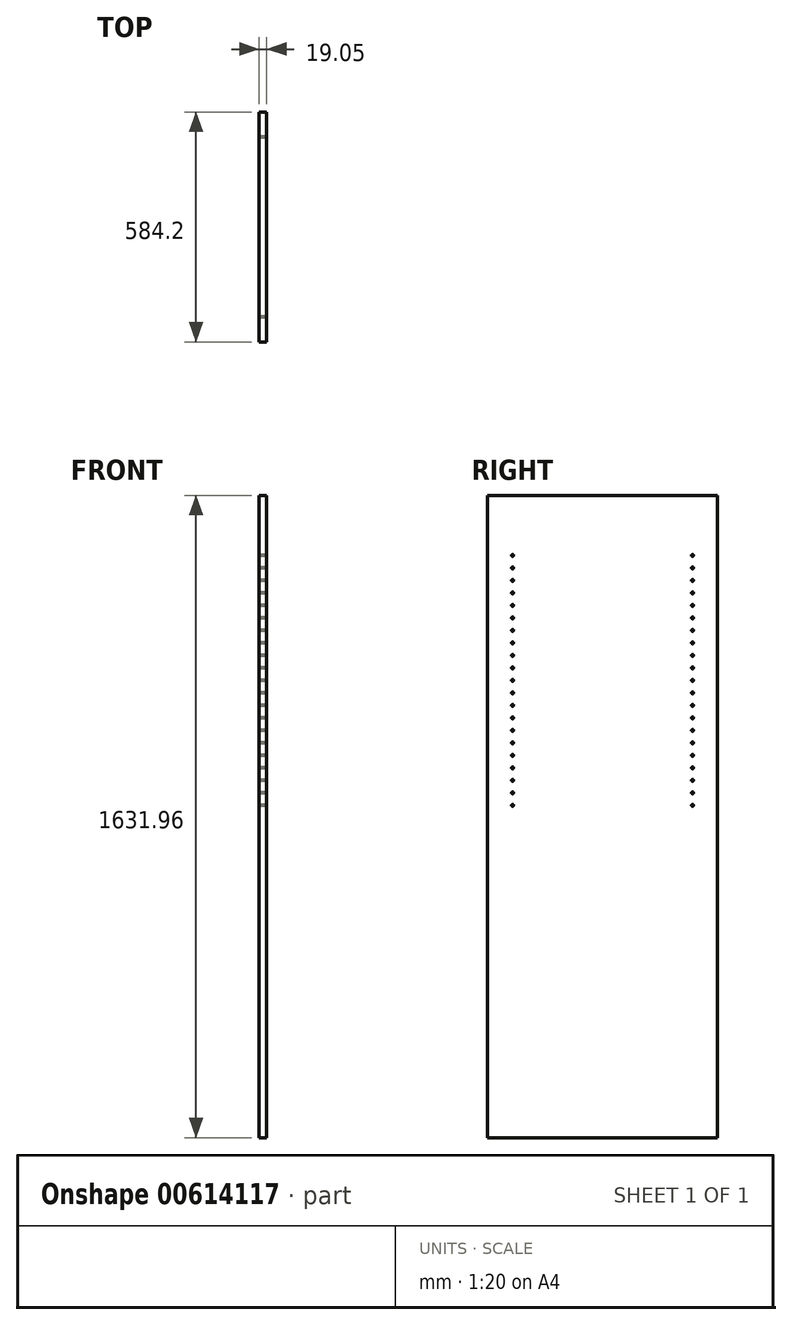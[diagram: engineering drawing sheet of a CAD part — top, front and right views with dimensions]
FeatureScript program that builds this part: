
annotation { "Feature Type Name" : "Feature", "Feature Type Description" : "" }
export const myFeature = defineFeature(function(context is Context, id is Id, definition is map)
    precondition{}
    {
        {
            var Q0;
            Q0=qCreatedBy(makeId("Right.planeOp"),FACE);
            var sketch = newSketch(context, id + "F0", { "sketchPlane" : qUnion([Q0])});
            skLineSegment(sketch, "E0.bottom", {"start": v(292.1, 815.98) * mm, "end": v(-292.1, 815.98) * mm});
            skLineSegment(sketch, "E0.top", {"start": v(292.1, -815.98) * mm, "end": v(-292.1, -815.98) * mm});
            skLineSegment(sketch, "E0.left", {"start": v(292.1, 815.98) * mm, "end": v(292.1, -815.98) * mm});
            skLineSegment(sketch, "E0.right", {"start": v(-292.1, 815.98) * mm, "end": v(-292.1, -815.98) * mm});
            skPoint(sketch, "E0.middle", {"position": v(0, 0) * mm});
            skSolve(sketch);
        }
        {
            var Q0;
            Q0=makeQuery(id+"F0.imprint","IMPRINT",FACE,{"disambiguationData":[TD([[makeQuery(id+"F0.imprint","IMPRINT",EDGE,{"derivedFrom":sQuery(id+"F0.wireOp",EDGE,"E0.bottom")}),1.0]])]});
            extrude(context, id + "F1", {"entities" : qUnion([Q0]), "depth" : 19.05 * mm, "offsetDistance" : 25.4 * mm});
        }
        {
            var Q0;
            Q0=makeQuery(id+"F1.opExtrude","CAP_FACE",FACE,{"disambiguationData":[OSD([sQuery(id+"F0.wireOp",EDGE,"E0.bottom"),sQuery(id+"F0.wireOp",EDGE,"E0.top"),sQuery(id+"F0.wireOp",EDGE,"E0.left"),sQuery(id+"F0.wireOp",EDGE,"E0.right")])],"isStart":false});
            var sketch = newSketch(context, id + "F2", { "sketchPlane" : qUnion([Q0])});
            skLineSegment(sketch, "E1", {"start": v(0, -815.98) * mm, "end": v(0, -53.97) * mm});
            skPoint(sketch, "E1.endSnap0", {"position": v(0, -815.98) * mm});
            skLineSegment(sketch, "E2", {"start": v(0, -53.97) * mm, "end": v(-292.1, -53.97) * mm});
            skLineSegment(sketch, "E3", {"start": v(0, 815.98) * mm, "end": v(0, 631.83) * mm});
            skPoint(sketch, "E3.endSnap0", {"position": v(0, 815.98) * mm});
            skLineSegment(sketch, "E4.bottom", {"start": v(228.6, 600.08) * mm, "end": v(-228.6, 600.08) * mm});
            skLineSegment(sketch, "E4.top", {"start": v(228.6, 663.58) * mm, "end": v(-228.6, 663.58) * mm});
            skLineSegment(sketch, "E4.left", {"start": v(228.6, 600.08) * mm, "end": v(228.6, 663.58) * mm});
            skLineSegment(sketch, "E4.right", {"start": v(-228.6, 600.08) * mm, "end": v(-228.6, 663.58) * mm});
            skPoint(sketch, "E4.middle", {"position": v(0, 631.83) * mm});
            skLineSegment(sketch, "E5", {"start": v(0, 600.08) * mm, "end": v(0, 536.58) * mm});
            skLineSegment(sketch, "E6.bottom", {"start": v(228.6, 568.33) * mm, "end": v(-228.6, 568.33) * mm});
            skLineSegment(sketch, "E6.top", {"start": v(228.6, 504.83) * mm, "end": v(-228.6, 504.83) * mm});
            skLineSegment(sketch, "E6.left", {"start": v(228.6, 568.33) * mm, "end": v(228.6, 504.83) * mm});
            skLineSegment(sketch, "E6.right", {"start": v(-228.6, 568.33) * mm, "end": v(-228.6, 504.83) * mm});
            skPoint(sketch, "E6.middle", {"position": v(0, 536.58) * mm});
            skLineSegment(sketch, "E7", {"start": v(0, 504.83) * mm, "end": v(0, 441.33) * mm});
            skLineSegment(sketch, "E8.bottom", {"start": v(228.6, 409.58) * mm, "end": v(-228.6, 409.58) * mm});
            skLineSegment(sketch, "E8.top", {"start": v(228.6, 473.08) * mm, "end": v(-228.6, 473.08) * mm});
            skLineSegment(sketch, "E8.left", {"start": v(228.6, 409.58) * mm, "end": v(228.6, 473.08) * mm});
            skLineSegment(sketch, "E8.right", {"start": v(-228.6, 409.58) * mm, "end": v(-228.6, 473.08) * mm});
            skPoint(sketch, "E8.middle", {"position": v(0, 441.33) * mm});
            skLineSegment(sketch, "E9", {"start": v(0, 409.58) * mm, "end": v(0, 346.08) * mm});
            skLineSegment(sketch, "E10.bottom", {"start": v(228.6, 377.83) * mm, "end": v(-228.6, 377.83) * mm});
            skLineSegment(sketch, "E10.top", {"start": v(228.6, 314.33) * mm, "end": v(-228.6, 314.33) * mm});
            skLineSegment(sketch, "E10.left", {"start": v(228.6, 377.83) * mm, "end": v(228.6, 314.33) * mm});
            skLineSegment(sketch, "E10.right", {"start": v(-228.6, 377.83) * mm, "end": v(-228.6, 314.33) * mm});
            skPoint(sketch, "E10.middle", {"position": v(0, 346.08) * mm});
            skLineSegment(sketch, "E11", {"start": v(0, 314.33) * mm, "end": v(0, 250.83) * mm});
            skLineSegment(sketch, "E12.bottom", {"start": v(228.6, 282.58) * mm, "end": v(-228.6, 282.58) * mm});
            skLineSegment(sketch, "E12.top", {"start": v(228.6, 219.08) * mm, "end": v(-228.6, 219.08) * mm});
            skLineSegment(sketch, "E12.left", {"start": v(228.6, 282.58) * mm, "end": v(228.6, 219.08) * mm});
            skLineSegment(sketch, "E12.right", {"start": v(-228.6, 282.58) * mm, "end": v(-228.6, 219.08) * mm});
            skPoint(sketch, "E12.middle", {"position": v(0, 250.83) * mm});
            skLineSegment(sketch, "E13", {"start": v(0, 219.08) * mm, "end": v(0, 155.58) * mm});
            skLineSegment(sketch, "E14.bottom", {"start": v(228.6, 123.83) * mm, "end": v(-228.6, 123.83) * mm});
            skLineSegment(sketch, "E14.top", {"start": v(228.6, 187.33) * mm, "end": v(-228.6, 187.33) * mm});
            skLineSegment(sketch, "E14.left", {"start": v(228.6, 123.83) * mm, "end": v(228.6, 187.33) * mm});
            skLineSegment(sketch, "E14.right", {"start": v(-228.6, 123.83) * mm, "end": v(-228.6, 187.33) * mm});
            skPoint(sketch, "E14.middle", {"position": v(0, 155.58) * mm});
            skLineSegment(sketch, "E15", {"start": v(0, 123.83) * mm, "end": v(0, 60.33) * mm});
            skLineSegment(sketch, "E16.bottom", {"start": v(228.6, 92.08) * mm, "end": v(-228.6, 92.08) * mm});
            skLineSegment(sketch, "E16.top", {"start": v(228.6, 28.58) * mm, "end": v(-228.6, 28.58) * mm});
            skLineSegment(sketch, "E16.left", {"start": v(228.6, 92.08) * mm, "end": v(228.6, 28.58) * mm});
            skLineSegment(sketch, "E16.right", {"start": v(-228.6, 92.08) * mm, "end": v(-228.6, 28.58) * mm});
            skPoint(sketch, "E16.middle", {"position": v(0, 60.33) * mm});
            skPoint(sketch, "E17", {"position": v(-228.6, 663.58) * mm});
            skPoint(sketch, "E18", {"position": v(-228.6, 631.83) * mm});
            skPoint(sketch, "E19", {"position": v(-228.6, 600.08) * mm});
            skPoint(sketch, "E20", {"position": v(-228.6, 568.33) * mm});
            skPoint(sketch, "E21", {"position": v(-228.6, 536.58) * mm});
            skPoint(sketch, "E22", {"position": v(-228.6, 504.83) * mm});
            skPoint(sketch, "E23", {"position": v(-228.6, 473.08) * mm});
            skPoint(sketch, "E24", {"position": v(-228.6, 441.33) * mm});
            skPoint(sketch, "E25", {"position": v(-228.6, 409.58) * mm});
            skPoint(sketch, "E26", {"position": v(-228.6, 377.83) * mm});
            skPoint(sketch, "E27", {"position": v(-228.6, 346.08) * mm});
            skPoint(sketch, "E28", {"position": v(-228.6, 314.33) * mm});
            skPoint(sketch, "E29", {"position": v(-228.6, 282.58) * mm});
            skPoint(sketch, "E30", {"position": v(-228.6, 250.83) * mm});
            skPoint(sketch, "E31", {"position": v(-228.6, 219.08) * mm});
            skPoint(sketch, "E32", {"position": v(-228.6, 187.33) * mm});
            skPoint(sketch, "E33", {"position": v(-228.6, 155.58) * mm});
            skPoint(sketch, "E34", {"position": v(-228.6, 123.83) * mm});
            skPoint(sketch, "E35", {"position": v(-228.6, 92.08) * mm});
            skPoint(sketch, "E36", {"position": v(-228.6, 60.33) * mm});
            skPoint(sketch, "E37", {"position": v(-228.6, 28.58) * mm});
            skPoint(sketch, "E38", {"position": v(228.6, 28.58) * mm});
            skPoint(sketch, "E39", {"position": v(228.6, 60.33) * mm});
            skPoint(sketch, "E40", {"position": v(228.6, 92.08) * mm});
            skPoint(sketch, "E41", {"position": v(228.6, 123.83) * mm});
            skPoint(sketch, "E42", {"position": v(228.6, 155.58) * mm});
            skPoint(sketch, "E43", {"position": v(228.6, 187.33) * mm});
            skPoint(sketch, "E44", {"position": v(228.6, 219.08) * mm});
            skPoint(sketch, "E45", {"position": v(228.6, 250.83) * mm});
            skPoint(sketch, "E46", {"position": v(228.6, 282.58) * mm});
            skPoint(sketch, "E47", {"position": v(228.6, 314.33) * mm});
            skPoint(sketch, "E48", {"position": v(228.6, 346.08) * mm});
            skPoint(sketch, "E49", {"position": v(228.6, 377.83) * mm});
            skPoint(sketch, "E50", {"position": v(228.6, 409.58) * mm});
            skPoint(sketch, "E51", {"position": v(228.6, 441.33) * mm});
            skPoint(sketch, "E52", {"position": v(228.6, 473.08) * mm});
            skPoint(sketch, "E53", {"position": v(228.6, 504.83) * mm});
            skPoint(sketch, "E54", {"position": v(228.6, 536.58) * mm});
            skPoint(sketch, "E55", {"position": v(228.6, 568.33) * mm});
            skPoint(sketch, "E56", {"position": v(228.6, 600.08) * mm});
            skPoint(sketch, "E57", {"position": v(228.6, 631.83) * mm});
            skPoint(sketch, "E58", {"position": v(228.6, 663.58) * mm});
            skSolve(sketch);
        }
        {
            var Q0;
            Q0=sQuery(id+"F2.wireOp",VERTEX,"E17");
            var Q1;
            Q1=sQuery(id+"F2.wireOp",VERTEX,"E18");
            var Q2;
            Q2=sQuery(id+"F2.wireOp",VERTEX,"E19");
            var Q3;
            Q3=sQuery(id+"F2.wireOp",VERTEX,"E20");
            var Q4;
            Q4=sQuery(id+"F2.wireOp",VERTEX,"E21");
            var Q5;
            Q5=sQuery(id+"F2.wireOp",VERTEX,"E22");
            var Q6;
            Q6=sQuery(id+"F2.wireOp",VERTEX,"E23");
            var Q7;
            Q7=sQuery(id+"F2.wireOp",VERTEX,"E24");
            var Q8;
            Q8=sQuery(id+"F2.wireOp",VERTEX,"E25");
            var Q9;
            Q9=sQuery(id+"F2.wireOp",VERTEX,"E26");
            var Q10;
            Q10=sQuery(id+"F2.wireOp",VERTEX,"E27");
            var Q11;
            Q11=sQuery(id+"F2.wireOp",VERTEX,"E28");
            var Q12;
            Q12=sQuery(id+"F2.wireOp",VERTEX,"E29");
            var Q13;
            Q13=sQuery(id+"F2.wireOp",VERTEX,"E30");
            var Q14;
            Q14=sQuery(id+"F2.wireOp",VERTEX,"E31");
            var Q15;
            Q15=sQuery(id+"F2.wireOp",VERTEX,"E32");
            var Q16;
            Q16=sQuery(id+"F2.wireOp",VERTEX,"E33");
            var Q17;
            Q17=sQuery(id+"F2.wireOp",VERTEX,"E34");
            var Q18;
            Q18=sQuery(id+"F2.wireOp",VERTEX,"E35");
            var Q19;
            Q19=sQuery(id+"F2.wireOp",VERTEX,"E36");
            var Q20;
            Q20=sQuery(id+"F2.wireOp",VERTEX,"E37");
            var Q21;
            Q21=sQuery(id+"F2.wireOp",VERTEX,"E58");
            var Q22;
            Q22=sQuery(id+"F2.wireOp",VERTEX,"E57");
            var Q23;
            Q23=sQuery(id+"F2.wireOp",VERTEX,"E56");
            var Q24;
            Q24=sQuery(id+"F2.wireOp",VERTEX,"E55");
            var Q25;
            Q25=sQuery(id+"F2.wireOp",VERTEX,"E54");
            var Q26;
            Q26=sQuery(id+"F2.wireOp",VERTEX,"E53");
            var Q27;
            Q27=sQuery(id+"F2.wireOp",VERTEX,"E52");
            var Q28;
            Q28=sQuery(id+"F2.wireOp",VERTEX,"E51");
            var Q29;
            Q29=sQuery(id+"F2.wireOp",VERTEX,"E50");
            var Q30;
            Q30=sQuery(id+"F2.wireOp",VERTEX,"E49");
            var Q31;
            Q31=sQuery(id+"F2.wireOp",VERTEX,"E48");
            var Q32;
            Q32=sQuery(id+"F2.wireOp",VERTEX,"E47");
            var Q33;
            Q33=sQuery(id+"F2.wireOp",VERTEX,"E46");
            var Q34;
            Q34=sQuery(id+"F2.wireOp",VERTEX,"E45");
            var Q35;
            Q35=sQuery(id+"F2.wireOp",VERTEX,"E44");
            var Q36;
            Q36=sQuery(id+"F2.wireOp",VERTEX,"E43");
            var Q37;
            Q37=sQuery(id+"F2.wireOp",VERTEX,"E42");
            var Q38;
            Q38=sQuery(id+"F2.wireOp",VERTEX,"E41");
            var Q39;
            Q39=sQuery(id+"F2.wireOp",VERTEX,"E40");
            var Q40;
            Q40=sQuery(id+"F2.wireOp",VERTEX,"E39");
            var Q41;
            Q41=sQuery(id+"F2.wireOp",VERTEX,"E38");
            var Q42;
            Q42=makeQuery(id+"F1.opExtrude","SWEPT_BODY",BODY,{"disambiguationData":[OSD([sQuery(id+"F0.wireOp",EDGE,"E0.bottom"),sQuery(id+"F0.wireOp",EDGE,"E0.top"),sQuery(id+"F0.wireOp",EDGE,"E0.left"),sQuery(id+"F0.wireOp",EDGE,"E0.right")])]});
            hole(context, id + "F3", {"style" : HoleStyle.SIMPLE, "endStyle" : HoleEndStyle.BLIND, "holeDiameter" : 5 * mm, "majorDiameter" : 6.35 * mm, "holeDepth" : 14.22 * mm, "isTappedThrough" : true, "tappedDepth" : 12.7 * mm, "tapClearance" : 3, "startFromSketch" : true, "locations" : qUnion([Q0, Q1, Q2, Q3, Q4, Q5, Q6, Q7, Q8, Q9, Q10, Q11, Q12, Q13, Q14, Q15, Q16, Q17, Q18, Q19, Q20, Q21, Q22, Q23, Q24, Q25, Q26, Q27, Q28, Q29, Q30, Q31, Q32, Q33, Q34, Q35, Q36, Q37, Q38, Q39, Q40, Q41]), "scope" : qUnion([Q42])});
        }
    });
